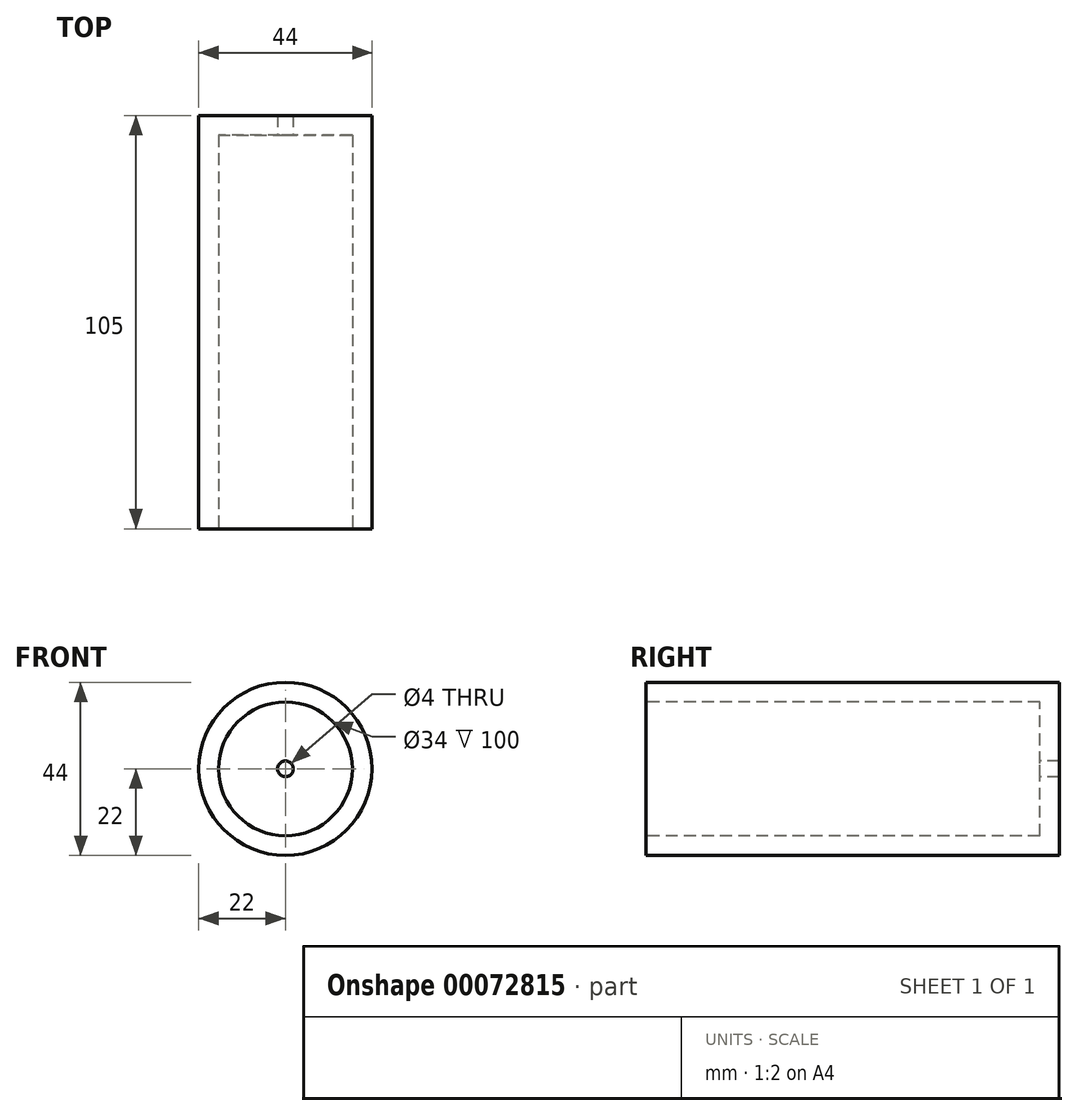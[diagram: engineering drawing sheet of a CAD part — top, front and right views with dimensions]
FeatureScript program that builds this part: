
annotation { "Feature Type Name" : "Feature", "Feature Type Description" : "" }
export const myFeature = defineFeature(function(context is Context, id is Id, definition is map)
    precondition{}
    {
        {
            var Q0;
            Q0=qCreatedBy(makeId("Top.planeOp"),FACE);
            var sketch = newSketch(context, id + "F0", { "sketchPlane" : qUnion([Q0])});
            skLineSegment(sketch, "E0", {"start": v(0, -71.7) * mm, "end": v(0, 73.63) * mm, "construction": true});
            skLineSegment(sketch, "E1", {"start": v(2, 56.81) * mm, "end": v(2, 51.81) * mm});
            skLineSegment(sketch, "E2", {"start": v(2, 51.81) * mm, "end": v(17, 51.81) * mm});
            skLineSegment(sketch, "E3", {"start": v(17, 51.81) * mm, "end": v(17, -48.19) * mm});
            skLineSegment(sketch, "E4", {"start": v(17, -48.19) * mm, "end": v(22, -48.19) * mm});
            skLineSegment(sketch, "E5", {"start": v(22, -48.19) * mm, "end": v(22, 56.81) * mm});
            skLineSegment(sketch, "E6", {"start": v(22, 56.81) * mm, "end": v(2, 56.81) * mm});
            skSolve(sketch);
        }
        {
            var Q0;
            Q0=makeQuery(id+"F0.imprint","IMPRINT",FACE,{"disambiguationData":[TD([[makeQuery(id+"F0.imprint","IMPRINT",EDGE,{"derivedFrom":sQuery(id+"F0.wireOp",EDGE,"E1")}),1.0]])]});
            var Q1;
            Q1=sQuery(id+"F0.wireOp",EDGE,"E0");
            revolve(context, id + "F1", {"entities" : qUnion([Q0]), "axis" : qUnion([Q1]), "revolveType" : RevolveType.FULL});
        }
    });
